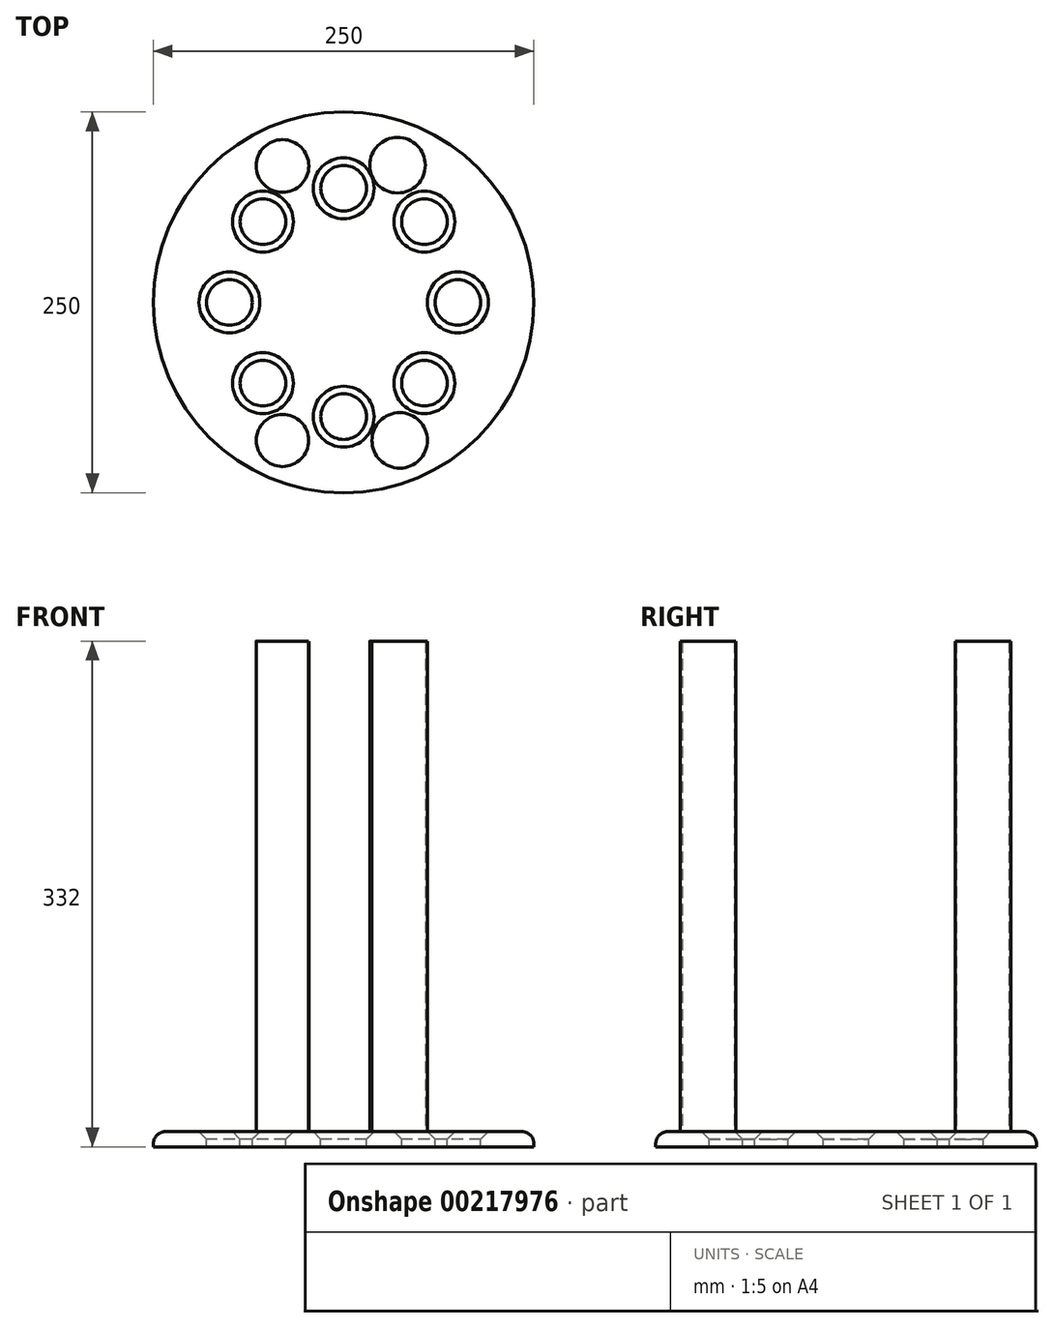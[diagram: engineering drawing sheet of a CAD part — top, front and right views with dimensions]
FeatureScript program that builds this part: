
annotation { "Feature Type Name" : "Feature", "Feature Type Description" : "" }
export const myFeature = defineFeature(function(context is Context, id is Id, definition is map)
    precondition{}
    {
        {
            var Q0;
            Q0=qCreatedBy(makeId("Top.planeOp"),FACE);
            var sketch = newSketch(context, id + "F0", { "sketchPlane" : qUnion([Q0])});
            skCircle(sketch, "E0", {"center": v(0, 0) * mm, "radius": 125 * mm});
            skSolve(sketch);
        }
        {
            var Q0;
            Q0=makeQuery(id+"F0.imprint","IMPRINT",FACE,{"disambiguationData":[TD([[makeQuery(id+"F0.imprint","IMPRINT",EDGE,{"derivedFrom":sQuery(id+"F0.wireOp",EDGE,"E0")}),1.0]])]});
            var sketch = newSketch(context, id + "F1", { "sketchPlane" : qUnion([Q0])});
            skCircle(sketch, "E1", {"center": v(0, 75) * mm, "radius": 15 * mm});
            skCircle(sketch, "E2.1.0", {"center": v(-53.03, 53.03) * mm, "radius": 15 * mm});
            skCircle(sketch, "E2.2.0", {"center": v(-75, 0) * mm, "radius": 15 * mm});
            skCircle(sketch, "E2.3.0", {"center": v(-53.03, -53.03) * mm, "radius": 15 * mm});
            skCircle(sketch, "E2.4.0", {"center": v(0, -75) * mm, "radius": 15 * mm});
            skCircle(sketch, "E2.5.0", {"center": v(53.03, -53.03) * mm, "radius": 15 * mm});
            skCircle(sketch, "E2.6.0", {"center": v(75, 0) * mm, "radius": 15 * mm});
            skCircle(sketch, "E2.7.0", {"center": v(53.03, 53.03) * mm, "radius": 15 * mm});
            skPoint(sketch, "E2.center", {"position": v(0, 0) * mm});
            skSolve(sketch);
        }
        {
            var Q0;
            Q0=makeQuery(id+"F1.imprint","IMPRINT",FACE,{"disambiguationData":[TD([[makeQuery(id+"F1.imprint","IMPRINT",EDGE,{"derivedFrom":sQuery(id+"F1.wireOp",EDGE,"E1")}),-1.0]])]});
            extrude(context, id + "F2", {"entities" : qUnion([Q0]), "oppositeDirection" : true, "depth" : 10 * mm});
        }
        {
            var Q0;
            Q0=makeQuery(id+"F2.opExtrude","CAP_EDGE",EDGE,{"disambiguationData":[OSD([sQuery(id+"F0.wireOp",EDGE,"E0")])],"isStart":true});
            fillet(context, id + "F3", {"entities" : qUnion([Q0]), "radius" : 8 * mm, "tangentPropagation" : true, "allowEdgeOverflow" : false});
        }
        {
            var Q0;
            Q0=makeQuery(id+"F2.opExtrude","CAP_EDGE",EDGE,{"disambiguationData":[OSD([sQuery(id+"F1.wireOp",EDGE,"E2.1.0")])],"isStart":true});
            var Q1;
            Q1=makeQuery(id+"F2.opExtrude","CAP_EDGE",EDGE,{"disambiguationData":[OSD([sQuery(id+"F1.wireOp",EDGE,"E1")])],"isStart":true});
            var Q2;
            Q2=makeQuery(id+"F2.opExtrude","CAP_EDGE",EDGE,{"disambiguationData":[OSD([sQuery(id+"F1.wireOp",EDGE,"E2.2.0")])],"isStart":true});
            var Q3;
            Q3=makeQuery(id+"F2.opExtrude","CAP_EDGE",EDGE,{"disambiguationData":[OSD([sQuery(id+"F1.wireOp",EDGE,"E2.7.0")])],"isStart":true});
            var Q4;
            Q4=makeQuery(id+"F2.opExtrude","CAP_EDGE",EDGE,{"disambiguationData":[OSD([sQuery(id+"F1.wireOp",EDGE,"E2.3.0")])],"isStart":true});
            var Q5;
            Q5=makeQuery(id+"F2.opExtrude","CAP_EDGE",EDGE,{"disambiguationData":[OSD([sQuery(id+"F1.wireOp",EDGE,"E2.4.0")])],"isStart":true});
            var Q6;
            Q6=makeQuery(id+"F2.opExtrude","CAP_EDGE",EDGE,{"disambiguationData":[OSD([sQuery(id+"F1.wireOp",EDGE,"E2.5.0")])],"isStart":true});
            var Q7;
            Q7=makeQuery(id+"F2.opExtrude","CAP_EDGE",EDGE,{"disambiguationData":[OSD([sQuery(id+"F1.wireOp",EDGE,"E2.6.0")])],"isStart":true});
            chamfer(context, id + "F4", {"entities" : qUnion([Q0, Q1, Q2, Q3, Q4, Q5, Q6, Q7]), "width" : 5 * mm, "tangentPropagation" : true});
        }
        {
            var Q0;
            Q0=makeQuery(id+"F0.imprint","IMPRINT",FACE,{"disambiguationData":[TD([[makeQuery(id+"F0.imprint","IMPRINT",EDGE,{"derivedFrom":sQuery(id+"F0.wireOp",EDGE,"E0")}),1.0]])]});
            var sketch = newSketch(context, id + "F5", { "sketchPlane" : qUnion([Q0])});
            skCircle(sketch, "E3", {"center": v(-40.16, 89.65) * mm, "radius": 17.32 * mm});
            skCircle(sketch, "E4", {"center": v(35.38, 90.13) * mm, "radius": 18.27 * mm});
            skCircle(sketch, "E5", {"center": v(-40.16, -90.6) * mm, "radius": 17.15 * mm});
            skCircle(sketch, "E6", {"center": v(36.82, -90.6) * mm, "radius": 18.2 * mm});
            skSolve(sketch);
        }
        {
            var Q0;
            Q0=makeQuery(id+"F5.imprint","IMPRINT",FACE,{"disambiguationData":[TD([[makeQuery(id+"F5.imprint","IMPRINT",EDGE,{"derivedFrom":sQuery(id+"F5.wireOp",EDGE,"E5")}),1.0]])]});
            var Q1;
            Q1=makeQuery(id+"F5.imprint","IMPRINT",FACE,{"disambiguationData":[TD([[makeQuery(id+"F5.imprint","IMPRINT",EDGE,{"derivedFrom":sQuery(id+"F5.wireOp",EDGE,"E6")}),1.0]])]});
            var Q2;
            Q2=makeQuery(id+"F5.imprint","IMPRINT",FACE,{"disambiguationData":[TD([[makeQuery(id+"F5.imprint","IMPRINT",EDGE,{"derivedFrom":sQuery(id+"F5.wireOp",EDGE,"E4")}),1.0]])]});
            var Q3;
            Q3=makeQuery(id+"F5.imprint","IMPRINT",FACE,{"disambiguationData":[TD([[makeQuery(id+"F5.imprint","IMPRINT",EDGE,{"derivedFrom":sQuery(id+"F5.wireOp",EDGE,"E3")}),1.0]])]});
            extrude(context, id + "F6", {"entities" : qUnion([Q0, Q1, Q2, Q3]), "operationType" : NewBodyOperationType.ADD, "depth" : 322 * mm});
        }
    });
